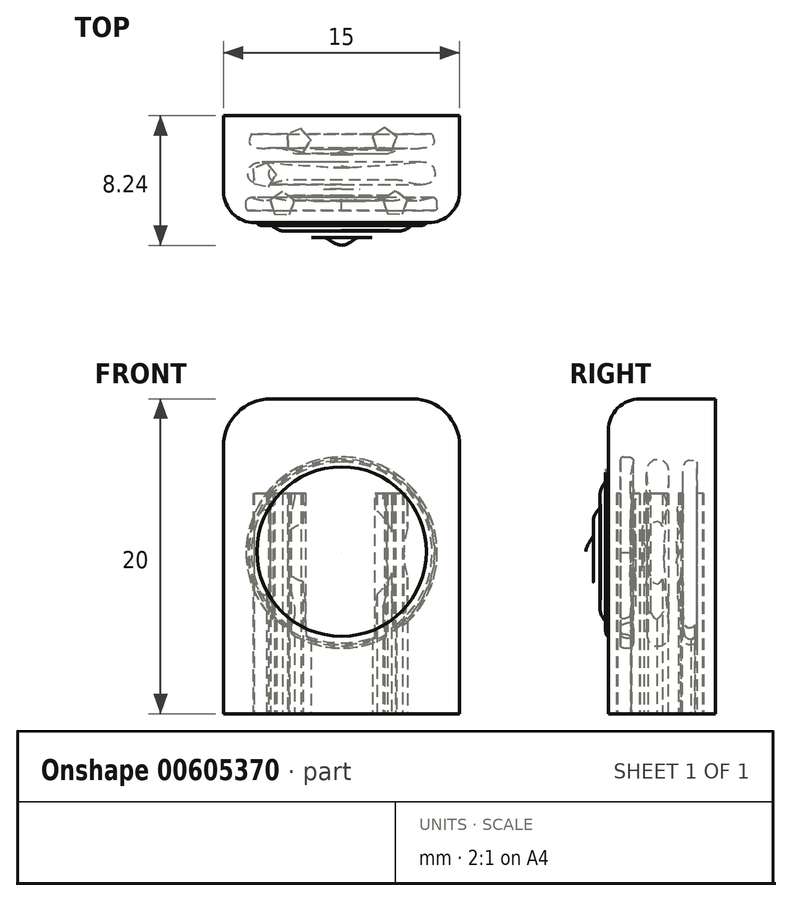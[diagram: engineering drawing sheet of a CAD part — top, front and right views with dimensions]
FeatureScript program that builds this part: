
annotation { "Feature Type Name" : "Feature", "Feature Type Description" : "" }
export const myFeature = defineFeature(function(context is Context, id is Id, definition is map)
    precondition{}
    {
        {
            var Q0;
            Q0=qCreatedBy(makeId("Front.planeOp"),FACE);
            var sketch = newSketch(context, id + "F0", { "sketchPlane" : qUnion([Q0])});
            skLineSegment(sketch, "E0", {"start": v(0, 0) * mm, "end": v(0, 17) * mm});
            skLineSegment(sketch, "E1", {"start": v(-3, 20) * mm, "end": v(-12, 20) * mm});
            skLineSegment(sketch, "E2", {"start": v(-15, 17) * mm, "end": v(-15, 0) * mm});
            skLineSegment(sketch, "E3", {"start": v(-15, 0) * mm, "end": v(0, 0) * mm});
            skPoint(sketch, "E4.visualSharp", {"position": v(-15, 20) * mm});
            skArc(sketch, "E4.filletArc", {"start": v(-12, 20) * mm, "mid": v(-14.12, 19.12) * mm, "end": v(-15, 17) * mm});
            skPoint(sketch, "E5.visualSharp", {"position": v(0, 20) * mm});
            skArc(sketch, "E5.filletArc", {"start": v(0, 17) * mm, "mid": v(-0.88, 19.12) * mm, "end": v(-3, 20) * mm});
            skSolve(sketch);
        }
        {
            var Q0;
            Q0=makeQuery(id+"F0.imprint","IMPRINT",FACE,{"disambiguationData":[TD([[makeQuery(id+"F0.imprint","IMPRINT",EDGE,{"derivedFrom":sQuery(id+"F0.wireOp",EDGE,"E0")}),1.0]])]});
            extrude(context, id + "F1", {"entities" : qUnion([Q0]), "depth" : 1.8 * mm, "offsetDistance" : 25 * mm, "hasSecondDirection" : true, "secondDirectionOppositeDirection" : true, "secondDirectionDepth" : 5 * mm});
        }
        {
            var Q0;
            Q0=sQuery(id+"F0.wireOp",EDGE,"E3");
            cPoint(context, id + "F2", {"entities" : qUnion([Q0]), "parameter" : 0.5});
        }
        {
            var Q0;
            Q0=qCreatedBy(makeId("Right.planeOp"),FACE);
            var Q1;
            Q1 = qCreatedBy(id + "F2" ,VERTEX);
            cPlane(context, id + "F3", {"entities" : qUnion([Q0, Q1]), "cplaneType" : CPlaneType.PLANE_POINT, "offset" : 25 * mm, "width" : 150 * mm, "height" : 150 * mm});
        }
        {
            var Q0;
            Q0=qCreatedBy(id+"F3.planeOp",FACE);
            var sketch = newSketch(context, id + "F4", { "sketchPlane" : qUnion([Q0])});
            skLineSegment(sketch, "E6", {"start": v(0, 10.24) * mm, "end": v(0.66, 10.24) * mm, "construction": true});
            skLineSegment(sketch, "E7", {"start": v(-0.14, 10.25) * mm, "end": v(-1.04, 10.25) * mm});
            skLineSegment(sketch, "E8", {"start": v(-0.5, 16.31) * mm, "end": v(-0.84, 16.31) * mm});
            skLineSegment(sketch, "E9", {"start": v(-1.04, 16.11) * mm, "end": v(-1.04, 10.25) * mm});
            skFitSpline(sketch, "E10", {"points": [v(-0.09, 16.31) * mm, v(-0.39, 14.91) * mm, v(-0.09, 13.74) * mm, v(-0.42, 12.03) * mm, v(-0.14, 10.25) * mm], "startDerivative": vector(-1.81, -5.8) * mm, "endDerivative": vector(1.79, -6.54) * mm});
            skPoint(sketch, "E11.visualSharp", {"position": v(-1.04, 16.31) * mm});
            skArc(sketch, "E11.filletArc", {"start": v(-0.84, 16.31) * mm, "mid": v(-0.98, 16.25) * mm, "end": v(-1.04, 16.11) * mm});
            skArc(sketch, "E12.filletArc", {"start": v(-0.21, 15.92) * mm, "mid": v(-0.26, 16.19) * mm, "end": v(-0.5, 16.31) * mm});
            skPoint(sketch, "E13.2.internal.snap0", {"position": v(0.33, 10.24) * mm});
            skPoint(sketch, "E13.3.internal.snap0", {"position": v(0.33, 10.24) * mm});
            skLineSegment(sketch, "E14", {"start": v(0.66, 10.24) * mm, "end": v(5.34, 10.24) * mm, "construction": true});
            skFitSpline(sketch, "E15", {"points": [v(0.86, 10.24) * mm, v(0.33, 11.43) * mm, v(0.9, 13.61) * mm, v(0.66, 14.9) * mm, v(0.93, 16.08) * mm, v(1.83, 15.98) * mm, v(2, 14.7) * mm, v(1.85, 13) * mm, v(1.78, 11.47) * mm, v(1.8, 10.24) * mm], "startDerivative": vector(-7.53, 9.77) * mm, "endDerivative": vector(4, -11.35) * mm});
            skFitSpline(sketch, "E16", {"points": [v(2.73, 10.24) * mm, v(2.54, 11.1) * mm, v(2.85, 11.9) * mm, v(2.58, 12.9) * mm, v(2.9, 14.01) * mm, v(2.92, 15.09) * mm, v(3.17, 16.06) * mm, v(3.82, 15.98) * mm], "startDerivative": vector(-2.72, 6.38) * mm, "endDerivative": vector(6.23, -2.37) * mm});
            skLineSegment(sketch, "E17", {"start": v(3.82, 15.98) * mm, "end": v(3.82, 10.24) * mm});
            skLineSegment(sketch, "E18", {"start": v(3.82, 10.24) * mm, "end": v(2.73, 10.24) * mm});
            skLineSegment(sketch, "E19", {"start": v(1.8, 10.24) * mm, "end": v(0.86, 10.24) * mm});
            skSolve(sketch);
        }
        {
            var Q0;
            Q0 = qSketchRegion(id + "F4", true);
            var Q1;
            Q1=sQuery(id+"F4.wireOp",EDGE,"ba93ea39-379c-4a41-bd4f-08c2b1c5362b");
            var Q2;
            Q2=sQuery(id+"F4.wireOp",EDGE,"SMfypYfj-xhII-lgbw-IWvV-8gJfxbIXPVbl");
            var Q3;
            Q3=sQuery(id+"F4.wireOp",EDGE,"E14");
            revolve(context, id + "F5", {"operationType" : NewBodyOperationType.REMOVE, "entities" : qUnion([Q0]), "surfaceEntities" : qUnion([Q1, Q2]), "axis" : qUnion([Q3]), "revolveType" : RevolveType.FULL, "oppositeDirection" : true});
        }
        {
            var Q0;
            Q0=qCreatedBy(id+"F3.planeOp",FACE);
            var sketch = newSketch(context, id + "F6", { "sketchPlane" : qUnion([Q0])});
            skLineSegment(sketch, "E20", {"start": v(3.66, 10.3) * mm, "end": v(-3.7, 10.3) * mm, "construction": true});
            skLineSegment(sketch, "E21", {"start": v(-1.51, 10.3) * mm, "end": v(-1.51, 15.68) * mm});
            skLineSegment(sketch, "E22", {"start": v(-1.51, 10.3) * mm, "end": v(-3.24, 10.3) * mm});
            skFitSpline(sketch, "E23", {"points": [v(-3.24, 10.3) * mm, v(-2.74, 11.37) * mm, v(-2.72, 12.5) * mm, v(-2.32, 13.15) * mm, v(-2.34, 13.88) * mm, v(-2.15, 14.5) * mm, v(-1.95, 14.95) * mm, v(-1.51, 15.68) * mm], "startDerivative": vector(1.13, 9.78) * mm, "endDerivative": vector(12.26, -2.96) * mm});
            skSolve(sketch);
        }
        {
            var Q0;
            Q0=makeQuery(id+"F6.imprint","IMPRINT",FACE,{"disambiguationData":[TD([[makeQuery(id+"F6.imprint","IMPRINT",EDGE,{"derivedFrom":sQuery(id+"F6.wireOp",EDGE,"E21")}),1.0]])]});
            var Q1;
            Q1=sQuery(id+"F6.wireOp",EDGE,"E20");
            revolve(context, id + "F7", {"operationType" : NewBodyOperationType.ADD, "entities" : qUnion([Q0]), "axis" : qUnion([Q1]), "revolveType" : RevolveType.FULL});
        }
        {
            var Q0;
            Q0=makeQuery(id+"F1.opExtrude","SWEPT_FACE",FACE,{"disambiguationData":[OSD([sQuery(id+"F0.wireOp",EDGE,"E3")])]});
            var sketch = newSketch(context, id + "F8", { "sketchPlane" : qUnion([Q0])});
            skCircle(sketch, "E24", {"center": v(-4.1, 0.58) * mm, "radius": 0.65 * mm, "construction": true});
            skCircle(sketch, "E25", {"center": v(-12.45, -1.22) * mm, "radius": 0.65 * mm, "construction": true});
            skLineSegment(sketch, "E26.0", {"start": v(-4.86, 0.32) * mm, "end": v(-4.59, 1.22) * mm});
            skLineSegment(sketch, "E26.1", {"start": v(-4.59, 1.22) * mm, "end": v(-3.64, 1.24) * mm});
            skLineSegment(sketch, "E26.2", {"start": v(-3.64, 1.24) * mm, "end": v(-3.33, 0.35) * mm});
            skLineSegment(sketch, "E26.3", {"start": v(-3.33, 0.35) * mm, "end": v(-4.08, -0.22) * mm});
            skLineSegment(sketch, "E26.4", {"start": v(-4.08, -0.22) * mm, "end": v(-4.86, 0.32) * mm});
            skPoint(sketch, "E26.0.midPoint", {"position": v(-4.72, 0.77) * mm});
            skLineSegment(sketch, "E27.0", {"start": v(-12.15, -0.47) * mm, "end": v(-11.65, -1.27) * mm});
            skLineSegment(sketch, "E27.1", {"start": v(-11.65, -1.27) * mm, "end": v(-12.26, -2) * mm});
            skLineSegment(sketch, "E27.2", {"start": v(-12.26, -2) * mm, "end": v(-13.13, -1.64) * mm});
            skLineSegment(sketch, "E27.3", {"start": v(-13.13, -1.64) * mm, "end": v(-13.07, -0.7) * mm});
            skLineSegment(sketch, "E27.4", {"start": v(-13.07, -0.7) * mm, "end": v(-12.15, -0.47) * mm});
            skPoint(sketch, "E27.0.midPoint", {"position": v(-11.9, -0.87) * mm});
            skCircle(sketch, "E28", {"center": v(-10.26, -3.39) * mm, "radius": 0.65 * mm, "construction": true});
            skLineSegment(sketch, "E29.0", {"start": v(-9.96, -2.65) * mm, "end": v(-9.46, -3.45) * mm});
            skLineSegment(sketch, "E29.1", {"start": v(-9.46, -3.45) * mm, "end": v(-10.07, -4.17) * mm});
            skLineSegment(sketch, "E29.2", {"start": v(-10.07, -4.17) * mm, "end": v(-10.95, -3.81) * mm});
            skLineSegment(sketch, "E29.3", {"start": v(-10.95, -3.81) * mm, "end": v(-10.88, -2.87) * mm});
            skLineSegment(sketch, "E29.4", {"start": v(-10.88, -2.87) * mm, "end": v(-9.96, -2.65) * mm});
            skPoint(sketch, "E29.0.midPoint", {"position": v(-9.7, -3.05) * mm});
            skCircle(sketch, "E30", {"center": v(-11.27, 0.61) * mm, "radius": 0.65 * mm, "construction": true});
            skLineSegment(sketch, "E31.0", {"start": v(-12.03, 0.35) * mm, "end": v(-11.76, 1.25) * mm});
            skLineSegment(sketch, "E31.1", {"start": v(-11.76, 1.25) * mm, "end": v(-10.81, 1.27) * mm});
            skLineSegment(sketch, "E31.2", {"start": v(-10.81, 1.27) * mm, "end": v(-10.5, 0.38) * mm});
            skLineSegment(sketch, "E31.3", {"start": v(-10.5, 0.38) * mm, "end": v(-11.25, -0.19) * mm});
            skLineSegment(sketch, "E31.4", {"start": v(-11.25, -0.19) * mm, "end": v(-12.03, 0.35) * mm});
            skPoint(sketch, "E31.0.midPoint", {"position": v(-11.9, 0.8) * mm});
            skCircle(sketch, "E32", {"center": v(-4.78, -3.45) * mm, "radius": 0.65 * mm, "construction": true});
            skLineSegment(sketch, "E33.0", {"start": v(-5.54, -3.71) * mm, "end": v(-5.27, -2.8) * mm});
            skLineSegment(sketch, "E33.1", {"start": v(-5.27, -2.8) * mm, "end": v(-4.32, -2.79) * mm});
            skLineSegment(sketch, "E33.2", {"start": v(-4.32, -2.79) * mm, "end": v(-4.01, -3.68) * mm});
            skLineSegment(sketch, "E33.3", {"start": v(-4.01, -3.68) * mm, "end": v(-4.76, -4.25) * mm});
            skLineSegment(sketch, "E33.4", {"start": v(-4.76, -4.25) * mm, "end": v(-5.54, -3.71) * mm});
            skPoint(sketch, "E33.0.midPoint", {"position": v(-5.4, -3.26) * mm});
            skSolve(sketch);
        }
        {
            var Q0;
            {var subQ0=sQuery(id+"F8.wireOp",EDGE,"E26.2");Q0=makeQuery(id+"F8.imprint","IMPRINT",FACE,{"disambiguationData":[TD([[makeQuery(id+"F8.imprint","IMPRINT",EDGE,{"derivedFrom":subQ0}),-1.0]])]});}
            var Q1;
            Q1=makeQuery(id+"F8.imprint","IMPRINT",FACE,{"disambiguationData":[TD([[makeQuery(id+"F8.imprint","IMPRINT",EDGE,{"derivedFrom":sQuery(id+"F8.wireOp",EDGE,"E27.0")}),-1.0]])]});
            var Q2;
            Q2=makeQuery(id+"F8.imprint","IMPRINT",FACE,{"disambiguationData":[TD([[makeQuery(id+"F8.imprint","IMPRINT",EDGE,{"derivedFrom":sQuery(id+"F8.wireOp",EDGE,"E29.0")}),-1.0]])]});
            var Q3;
            Q3=makeQuery(id+"F8.imprint","IMPRINT",FACE,{"disambiguationData":[TD([[makeQuery(id+"F8.imprint","IMPRINT",EDGE,{"derivedFrom":sQuery(id+"F8.wireOp",EDGE,"E31.0")}),-1.0]])]});
            var Q4;
            Q4=makeQuery(id+"F8.imprint","IMPRINT",FACE,{"disambiguationData":[TD([[makeQuery(id+"F8.imprint","IMPRINT",EDGE,{"derivedFrom":sQuery(id+"F8.wireOp",EDGE,"E33.0")}),-1.0]])]});
            extrude(context, id + "F9", {"entities" : qUnion([Q0, Q1, Q2, Q3, Q4]), "operationType" : NewBodyOperationType.REMOVE, "oppositeDirection" : true, "depth" : 14 * mm, "offsetDistance" : 25 * mm});
        }
        {
            var Q0;
            Q0=makeQuery(id+"F1.opExtrude","CAP_EDGE",EDGE,{"disambiguationData":[OSD([sQuery(id+"F0.wireOp",EDGE,"E0")])],"isStart":false});
            var Q1;
            Q1=makeQuery(id+"F1.opExtrude","CAP_EDGE",EDGE,{"disambiguationData":[OSD([sQuery(id+"F0.wireOp",EDGE,"E5.filletArc")])],"isStart":false});
            var Q2;
            Q2=makeQuery(id+"F1.opExtrude","CAP_EDGE",EDGE,{"disambiguationData":[OSD([sQuery(id+"F0.wireOp",EDGE,"E1")])],"isStart":false});
            var Q3;
            Q3=makeQuery(id+"F1.opExtrude","CAP_EDGE",EDGE,{"disambiguationData":[OSD([sQuery(id+"F0.wireOp",EDGE,"E4.filletArc")])],"isStart":false});
            var Q4;
            Q4=makeQuery(id+"F1.opExtrude","CAP_EDGE",EDGE,{"disambiguationData":[OSD([sQuery(id+"F0.wireOp",EDGE,"E2")])],"isStart":false});
            fillet(context, id + "F10", {"entities" : qUnion([Q0, Q1, Q2, Q3, Q4]), "radius" : 2 * mm, "tangentPropagation" : true, "allowEdgeOverflow" : false});
        }
    });
